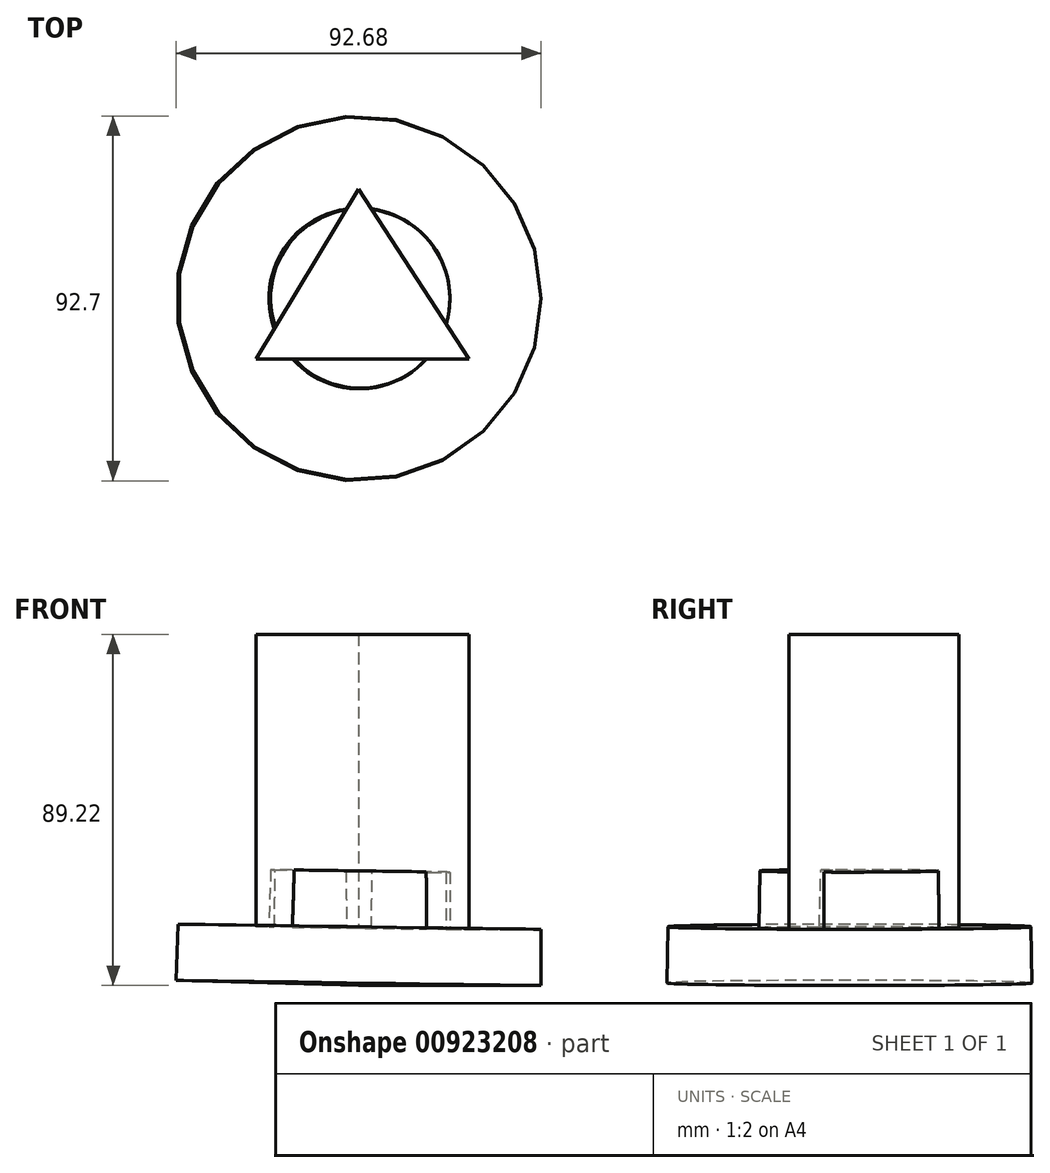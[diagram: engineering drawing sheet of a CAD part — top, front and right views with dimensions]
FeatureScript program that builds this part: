
annotation { "Feature Type Name" : "Feature", "Feature Type Description" : "" }
export const myFeature = defineFeature(function(context is Context, id is Id, definition is map)
    precondition{}
    {
        {
            var Q0;
            Q0=qCreatedBy(makeId("Front.planeOp"),FACE);
            var sketch = newSketch(context, id + "F0", { "sketchPlane" : qUnion([Q0])});
            skLineSegment(sketch, "E0", {"start": v(0, -14.27) * mm, "end": v(46.35, -14.27) * mm});
            skLineSegment(sketch, "E1", {"start": v(46.35, -14.27) * mm, "end": v(46.35, 0) * mm});
            skLineSegment(sketch, "E2", {"start": v(46.35, 0) * mm, "end": v(0, 0) * mm});
            skLineSegment(sketch, "E3", {"start": v(0, 0) * mm, "end": v(23.18, 0) * mm});
            skLineSegment(sketch, "E4", {"start": v(23.18, 0) * mm, "end": v(23.18, 14.53) * mm});
            skLineSegment(sketch, "E5", {"start": v(23.18, 14.53) * mm, "end": v(0, 14.53) * mm});
            skLineSegment(sketch, "E6", {"start": v(0, 14.53) * mm, "end": v(0, 14.53) * mm});
            skLineSegment(sketch, "E7", {"start": v(0.98, 55.43) * mm, "end": v(11.98, 55.43) * mm});
            skLineSegment(sketch, "E8", {"start": v(23.18, 14.53) * mm, "end": v(11.59, 14.53) * mm});
            skLineSegment(sketch, "E9", {"start": v(11.98, 55.43) * mm, "end": v(11.59, 14.53) * mm});
            skLineSegment(sketch, "E10", {"start": v(0.98, 55.43) * mm, "end": v(0, -14.27) * mm});
            skSolve(sketch);
        }
        {
            var Q0;
            {var subQ4=sQuery(id+"F0.wireOp",EDGE,"E4");Q0=makeQuery(id+"F0.imprint","IMPRINT",FACE,{"disambiguationData":[TD([[makeQuery(id+"F0.imprint","IMPRINT",EDGE,{"derivedFrom":subQ4}),1.0]])]});}
            var Q1;
            {var subQ4=sQuery(id+"F0.wireOp",EDGE,"E0");Q1=makeQuery(id+"F0.imprint","IMPRINT",FACE,{"disambiguationData":[TD([[makeQuery(id+"F0.imprint","IMPRINT",EDGE,{"derivedFrom":subQ4}),1.0]])]});}
            var Q2;
            {var subQ4=sQuery(id+"F0.wireOp",EDGE,"E7");Q2=makeQuery(id+"F0.imprint","IMPRINT",FACE,{"disambiguationData":[TD([[makeQuery(id+"F0.imprint","IMPRINT",EDGE,{"derivedFrom":subQ4}),-1.0]])]});}
            var Q3;
            Q3=sQuery(id+"F0.wireOp",EDGE,"E10");
            revolve(context, id + "F1", {"surfaceOperationType" : NewSurfaceOperationType.NEW, "entities" : qUnion([Q0, Q1, Q2]), "axis" : qUnion([Q3]), "revolveType" : RevolveType.FULL});
        }
        {
            var Q0;
            Q0=qCreatedBy(makeId("Top.planeOp"),FACE);
            var sketch = newSketch(context, id + "F2", { "sketchPlane" : qUnion([Q0])});
            skLineSegment(sketch, "E11", {"start": v(28.05, -15.4) * mm, "end": v(-26.1, -15.4) * mm});
            skLineSegment(sketch, "E12", {"start": v(-26.1, -15.4) * mm, "end": v(0, 27.81) * mm});
            skLineSegment(sketch, "E13", {"start": v(0, 27.81) * mm, "end": v(28.05, -15.4) * mm});
            skSolve(sketch);
        }
        {
            var Q0;
            Q0=makeQuery(id+"F2.imprint","IMPRINT",FACE,{"disambiguationData":[TD([[makeQuery(id+"F2.imprint","IMPRINT",EDGE,{"derivedFrom":sQuery(id+"F2.wireOp",EDGE,"E11")}),-1.0]])]});
            extrude(context, id + "F3", {"entities" : qUnion([Q0]), "operationType" : NewBodyOperationType.ADD, "depth" : 74.95 * mm, "offsetDistance" : 25.4 * mm});
        }
    });
